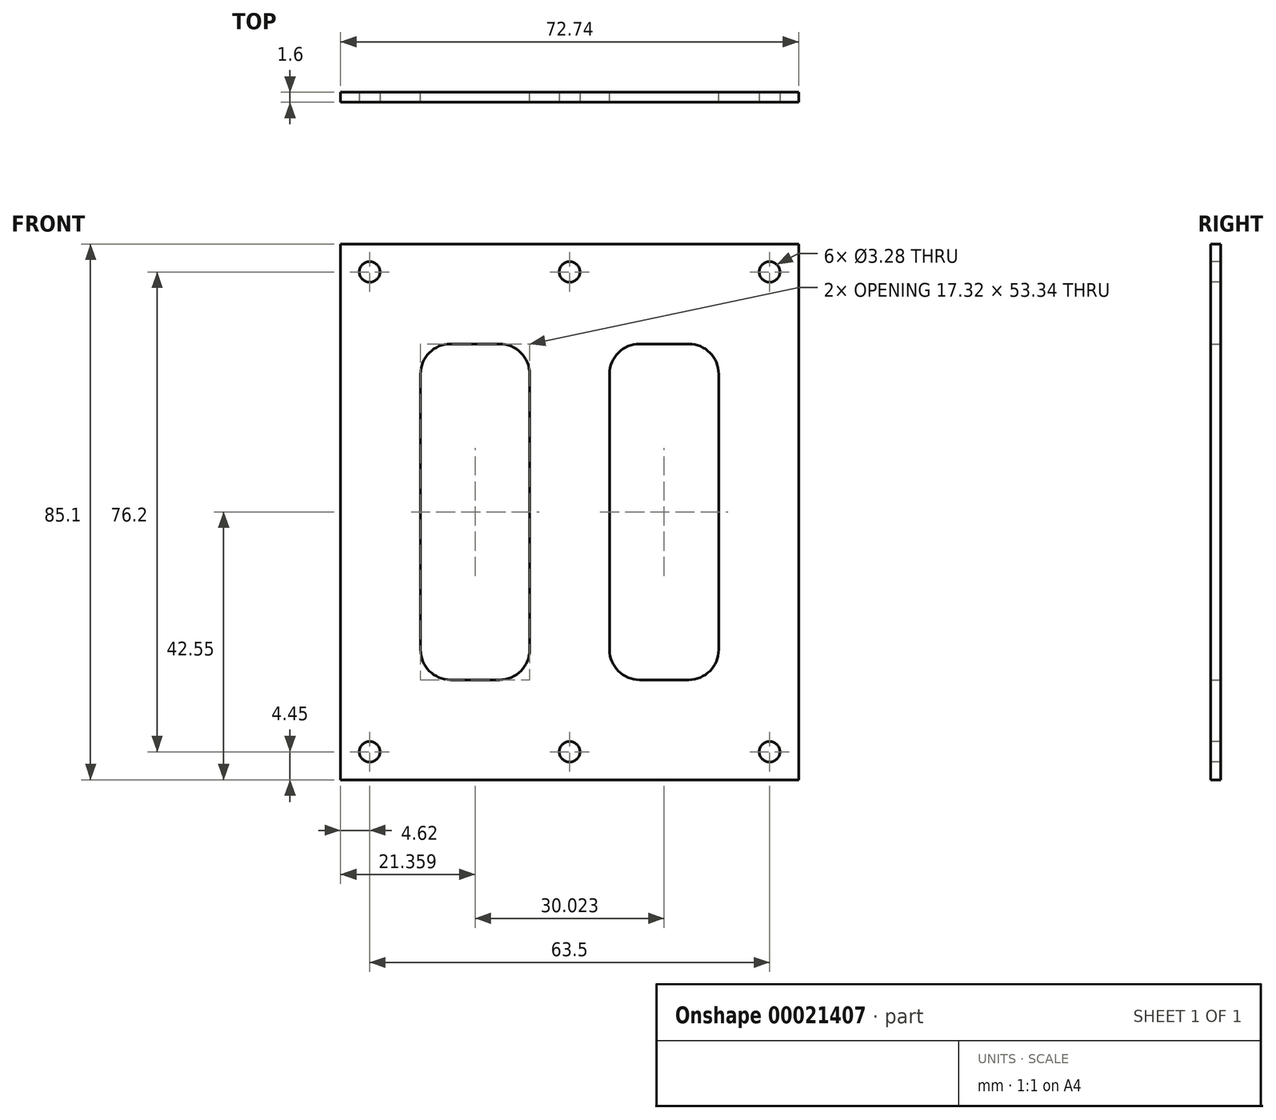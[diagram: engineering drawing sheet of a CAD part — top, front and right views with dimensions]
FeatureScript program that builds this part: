
annotation { "Feature Type Name" : "Feature", "Feature Type Description" : "" }
export const myFeature = defineFeature(function(context is Context, id is Id, definition is map)
    precondition{}
    {
        {
            var Q0;
            Q0=qCreatedBy(makeId("Front.planeOp"),FACE);
            var sketch = newSketch(context, id + "F0", { "sketchPlane" : qUnion([Q0])});
            skLineSegment(sketch, "E0.rect.bottom", {"start": v(-36.37, 42.55) * mm, "end": v(36.37, 42.55) * mm});
            skLineSegment(sketch, "E0.rect.top", {"start": v(-36.37, -42.55) * mm, "end": v(36.37, -42.55) * mm});
            skLineSegment(sketch, "E0.rect.left", {"start": v(-36.37, 42.55) * mm, "end": v(-36.37, -42.55) * mm});
            skLineSegment(sketch, "E0.rect.right", {"start": v(36.37, 42.55) * mm, "end": v(36.37, -42.55) * mm});
            skPoint(sketch, "E0.rect.middle", {"position": v(0, 0) * mm});
            skLineSegment(sketch, "E1.bottom", {"start": v(-23.67, 26.67) * mm, "end": v(-6.35, 26.67) * mm});
            skLineSegment(sketch, "E1.top", {"start": v(-23.67, -26.67) * mm, "end": v(-6.35, -26.67) * mm});
            skLineSegment(sketch, "E1.left", {"start": v(-23.67, 26.67) * mm, "end": v(-23.67, -26.67) * mm});
            skLineSegment(sketch, "E1.right", {"start": v(-6.35, 26.67) * mm, "end": v(-6.35, -26.67) * mm});
            skLineSegment(sketch, "E2", {"start": v(0, 0) * mm, "end": v(0, 53.83) * mm});
            skLineSegment(sketch, "E3", {"start": v(0, 0) * mm, "end": v(49, 0) * mm});
            skLineSegment(sketch, "E4.bottom", {"start": v(6.35, 26.67) * mm, "end": v(23.67, 26.67) * mm});
            skLineSegment(sketch, "E4.top", {"start": v(6.35, -26.67) * mm, "end": v(23.67, -26.67) * mm});
            skLineSegment(sketch, "E4.left", {"start": v(6.35, 26.67) * mm, "end": v(6.35, -26.67) * mm});
            skLineSegment(sketch, "E4.right", {"start": v(23.67, 26.67) * mm, "end": v(23.67, -26.67) * mm});
            skSolve(sketch);
        }
        {
            var Q0;
            {var subQ12=sQuery(id+"F0.wireOp",EDGE,"E0.rect.top");Q0=makeQuery(id+"F0.imprint","IMPRINT",FACE,{"disambiguationData":[TD([[makeQuery(id+"F0.imprint","IMPRINT",EDGE,{"derivedFrom":subQ12}),1.0]])]});}
            var Q1;
            {var subQ3=sQuery(id+"F0.wireOp",EDGE,"E4.bottom");Q1=makeQuery(id+"F0.imprint","IMPRINT",FACE,{"disambiguationData":[TD([[makeQuery(id+"F0.imprint","IMPRINT",EDGE,{"derivedFrom":subQ3}),1.0]])]});}
            extrude(context, id + "F1", {"entities" : qUnion([Q0, Q1]), "depth" : 1.6 * mm});
        }
        {
            var Q0;
            Q0=makeQuery(id+"F1.opExtrude","SWEPT_EDGE",EDGE,{"disambiguationData":[OSD([sQuery(id+"F0.wireOp",EDGE,"E4.bottom"),sQuery(id+"F0.wireOp",EDGE,"E4.right")])]});
            var Q1;
            Q1=makeQuery(id+"F1.opExtrude","SWEPT_EDGE",EDGE,{"disambiguationData":[OSD([sQuery(id+"F0.wireOp",EDGE,"E4.top"),sQuery(id+"F0.wireOp",EDGE,"E4.left")])]});
            var Q2;
            Q2=makeQuery(id+"F1.opExtrude","SWEPT_EDGE",EDGE,{"disambiguationData":[OSD([sQuery(id+"F0.wireOp",EDGE,"E4.bottom"),sQuery(id+"F0.wireOp",EDGE,"E4.left")])]});
            var Q3;
            Q3=makeQuery(id+"F1.opExtrude","SWEPT_EDGE",EDGE,{"disambiguationData":[OSD([sQuery(id+"F0.wireOp",EDGE,"E1.top"),sQuery(id+"F0.wireOp",EDGE,"E1.right")])]});
            var Q4;
            Q4=makeQuery(id+"F1.opExtrude","SWEPT_EDGE",EDGE,{"disambiguationData":[OSD([sQuery(id+"F0.wireOp",EDGE,"E1.bottom"),sQuery(id+"F0.wireOp",EDGE,"E1.right")])]});
            var Q5;
            Q5=makeQuery(id+"F1.opExtrude","SWEPT_EDGE",EDGE,{"disambiguationData":[OSD([sQuery(id+"F0.wireOp",EDGE,"E1.bottom"),sQuery(id+"F0.wireOp",EDGE,"E1.left")])]});
            var Q6;
            Q6=makeQuery(id+"F1.opExtrude","SWEPT_EDGE",EDGE,{"disambiguationData":[OSD([sQuery(id+"F0.wireOp",EDGE,"E4.top"),sQuery(id+"F0.wireOp",EDGE,"E4.right")])]});
            var Q7;
            Q7=makeQuery(id+"F1.opExtrude","SWEPT_EDGE",EDGE,{"disambiguationData":[OSD([sQuery(id+"F0.wireOp",EDGE,"E1.top"),sQuery(id+"F0.wireOp",EDGE,"E1.left")])]});
            fillet(context, id + "F2", {"entities" : qUnion([Q0, Q1, Q2, Q3, Q4, Q5, Q6, Q7]), "radius" : 4.78 * mm, "tangentPropagation" : true, "allowEdgeOverflow" : false});
        }
        {
            var Q0;
            Q0=makeQuery(id+"F1.opExtrude","CAP_FACE",FACE,{"disambiguationData":[OSD([sQuery(id+"F0.wireOp",EDGE,"E0.rect.bottom"),sQuery(id+"F0.wireOp",EDGE,"E0.rect.top"),sQuery(id+"F0.wireOp",EDGE,"E0.rect.left"),sQuery(id+"F0.wireOp",EDGE,"E0.rect.right"),sQuery(id+"F0.wireOp",EDGE,"E1.bottom"),sQuery(id+"F0.wireOp",EDGE,"E1.top"),sQuery(id+"F0.wireOp",EDGE,"E1.left"),sQuery(id+"F0.wireOp",EDGE,"E1.right"),sQuery(id+"F0.wireOp",EDGE,"E4.bottom"),sQuery(id+"F0.wireOp",EDGE,"E4.top"),sQuery(id+"F0.wireOp",EDGE,"E4.left"),sQuery(id+"F0.wireOp",EDGE,"E4.right")])],"isStart":false});
            var sketch = newSketch(context, id + "F3", { "sketchPlane" : qUnion([Q0])});
            skLineSegment(sketch, "E5.rect.bottom", {"start": v(-31.75, 38.1) * mm, "end": v(31.75, 38.1) * mm});
            skLineSegment(sketch, "E5.rect.top", {"start": v(-31.75, -38.1) * mm, "end": v(31.75, -38.1) * mm});
            skLineSegment(sketch, "E5.rect.left", {"start": v(-31.75, 38.1) * mm, "end": v(-31.75, -38.1) * mm});
            skLineSegment(sketch, "E5.rect.right", {"start": v(31.75, 38.1) * mm, "end": v(31.75, -38.1) * mm});
            skPoint(sketch, "E5.rect.middle", {"position": v(0, 0) * mm});
            skLineSegment(sketch, "E6", {"start": v(0, 0) * mm, "end": v(0, 38.1) * mm});
            skLineSegment(sketch, "E7", {"start": v(0, 0) * mm, "end": v(0, -38.1) * mm});
            skSolve(sketch);
        }
        {
            var Q0;
            Q0=sQuery(id+"F3.wireOp",VERTEX,"E5.rect.bottom.start");
            var Q1;
            Q1=sQuery(id+"F3.wireOp",VERTEX,"E6.end");
            var Q2;
            Q2=sQuery(id+"F3.wireOp",VERTEX,"E5.rect.right.start");
            var Q3;
            Q3=sQuery(id+"F3.wireOp",VERTEX,"E5.rect.right.end");
            var Q4;
            Q4=sQuery(id+"F3.wireOp",VERTEX,"E7.end");
            var Q5;
            Q5=sQuery(id+"F3.wireOp",VERTEX,"E5.rect.left.end");
            var Q6;
            Q6=makeQuery(id+"F1.opExtrude","SWEPT_BODY",BODY,{"disambiguationData":[OSD([sQuery(id+"F0.wireOp",EDGE,"E0.rect.bottom"),sQuery(id+"F0.wireOp",EDGE,"E0.rect.top"),sQuery(id+"F0.wireOp",EDGE,"E0.rect.left"),sQuery(id+"F0.wireOp",EDGE,"E0.rect.right"),sQuery(id+"F0.wireOp",EDGE,"E1.bottom"),sQuery(id+"F0.wireOp",EDGE,"E1.top"),sQuery(id+"F0.wireOp",EDGE,"E1.left"),sQuery(id+"F0.wireOp",EDGE,"E1.right"),sQuery(id+"F0.wireOp",EDGE,"E4.bottom"),sQuery(id+"F0.wireOp",EDGE,"E4.top"),sQuery(id+"F0.wireOp",EDGE,"E4.left"),sQuery(id+"F0.wireOp",EDGE,"E4.right")])]});
            hole(context, id + "F4", {"style" : HoleStyle.SIMPLE, "holeDiameter" : 3.28 * mm, "endStyle" : HoleEndStyle.THROUGH, "locations" : qUnion([Q0, Q1, Q2, Q3, Q4, Q5]), "scope" : qUnion([Q6])});
        }
    });
